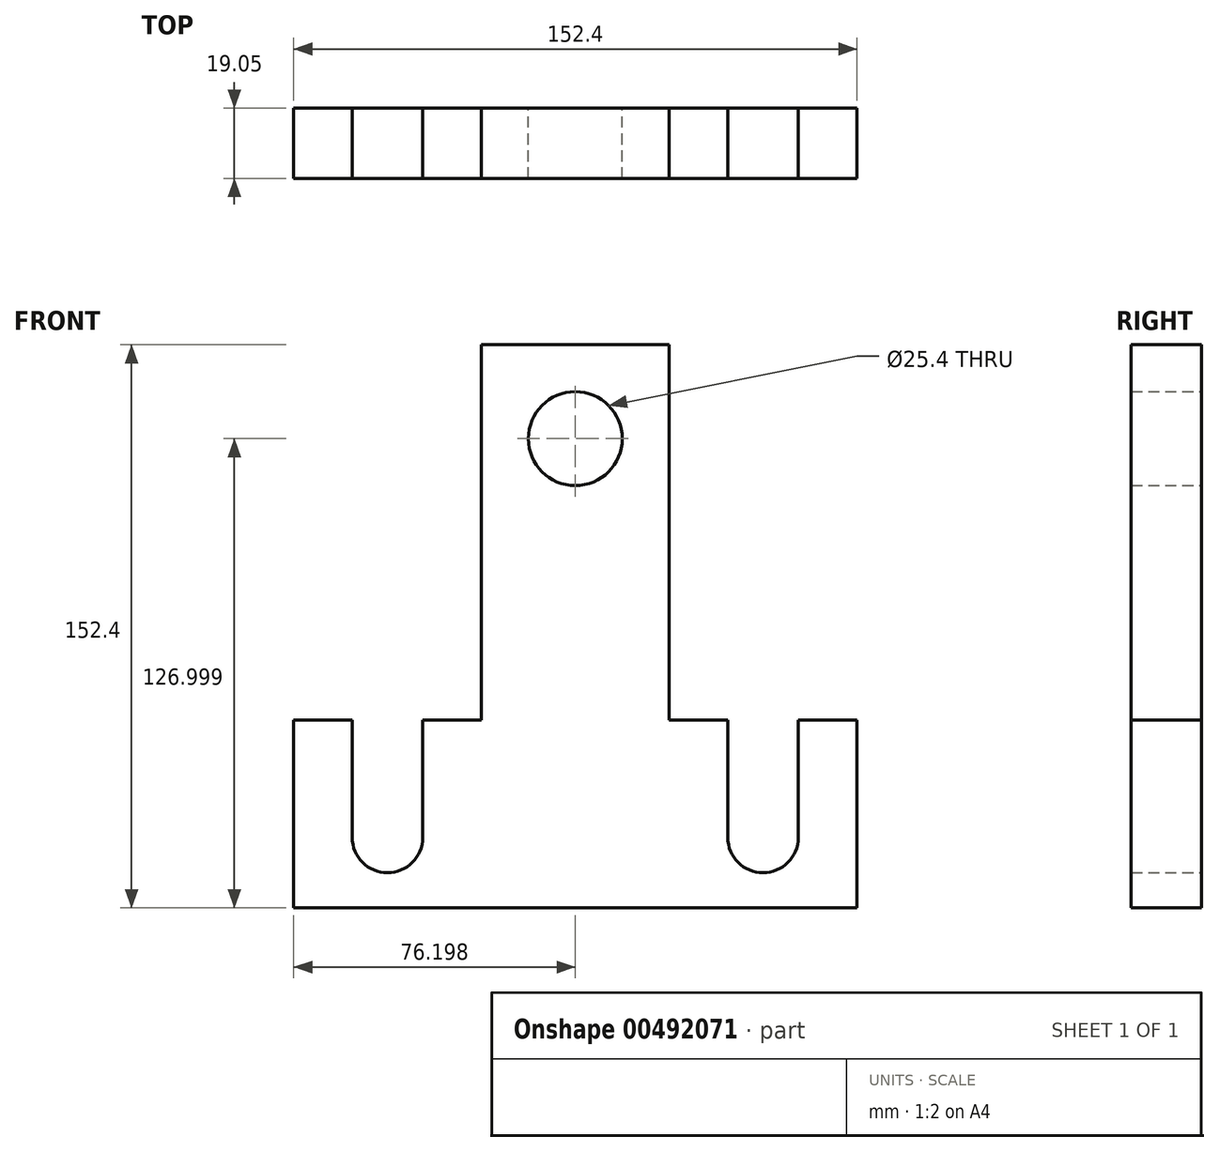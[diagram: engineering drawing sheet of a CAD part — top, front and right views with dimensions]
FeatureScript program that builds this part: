
annotation { "Feature Type Name" : "Feature", "Feature Type Description" : "" }
export const myFeature = defineFeature(function(context is Context, id is Id, definition is map)
    precondition{}
    {
        {
            var Q0;
            Q0=qCreatedBy(makeId("Front.planeOp"),FACE);
            var sketch = newSketch(context, id + "F0", { "sketchPlane" : qUnion([Q0])});
            skLineSegment(sketch, "E0.bottom", {"start": v(-186.96, -13.95) * mm, "end": v(-171.09, -13.95) * mm});
            skLineSegment(sketch, "E0.top", {"start": v(-288.56, -64.75) * mm, "end": v(-136.16, -64.75) * mm});
            skLineSegment(sketch, "E0.left", {"start": v(-186.96, 87.65) * mm, "end": v(-186.96, -13.95) * mm});
            skLineSegment(sketch, "E0.right", {"start": v(-136.16, -13.95) * mm, "end": v(-136.16, -64.75) * mm});
            skArc(sketch, "E1", {"start": v(-171.09, -45.7) * mm, "mid": v(-161.56, -55.23) * mm, "end": v(-152.04, -45.7) * mm});
            skLineSegment(sketch, "E2", {"start": v(-152.04, -45.7) * mm, "end": v(-152.04, -13.95) * mm});
            skLineSegment(sketch, "E3", {"start": v(-171.09, -13.95) * mm, "end": v(-171.09, -45.7) * mm});
            skLineSegment(sketch, "E4.trimOffspring", {"start": v(-152.04, -13.95) * mm, "end": v(-136.16, -13.95) * mm});
            skLineSegment(sketch, "E5.MirrorCS", {"start": v(-237.76, 87.65) * mm, "end": v(-237.76, -13.95) * mm});
            skLineSegment(sketch, "E6.MirrorCS", {"start": v(-288.56, -13.95) * mm, "end": v(-288.56, -64.75) * mm});
            skLineSegment(sketch, "E7.MirrorCS", {"start": v(-272.69, -13.95) * mm, "end": v(-288.56, -13.95) * mm});
            skLineSegment(sketch, "E8.MirrorCS", {"start": v(-272.69, -45.7) * mm, "end": v(-272.69, -13.95) * mm});
            skArc(sketch, "E9.MirrorCS", {"start": v(-253.64, -45.7) * mm, "mid": v(-263.16, -55.23) * mm, "end": v(-272.69, -45.7) * mm});
            skLineSegment(sketch, "E10.MirrorCS", {"start": v(-253.64, -13.95) * mm, "end": v(-253.64, -45.7) * mm});
            skLineSegment(sketch, "E11.MirrorCS", {"start": v(-237.76, -13.95) * mm, "end": v(-253.64, -13.95) * mm});
            skLineSegment(sketch, "E12", {"start": v(-237.76, 87.65) * mm, "end": v(-186.96, 87.65) * mm});
            skCircle(sketch, "E13", {"center": v(-212.36, 62.25) * mm, "radius": 12.7 * mm});
            skSolve(sketch);
        }
        {
            var Q0;
            Q0=makeQuery(id+"F0.imprint","IMPRINT",FACE,{"disambiguationData":[TD([[makeQuery(id+"F0.imprint","IMPRINT",EDGE,{"derivedFrom":sQuery(id+"F0.wireOp",EDGE,"E0.bottom")}),-1.0]])]});
            extrude(context, id + "F1", {"entities" : qUnion([Q0]), "depth" : 19.05 * mm});
        }
    });
